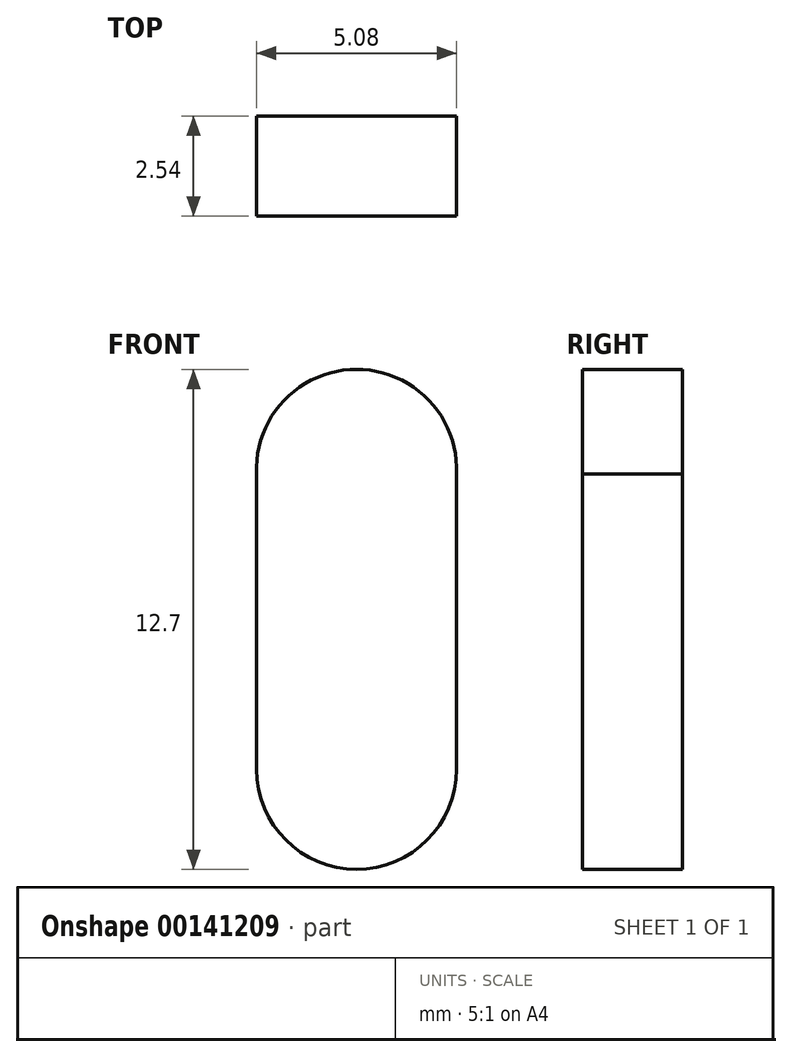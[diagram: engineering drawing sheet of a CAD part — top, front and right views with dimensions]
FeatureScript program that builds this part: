
annotation { "Feature Type Name" : "Feature", "Feature Type Description" : "" }
export const myFeature = defineFeature(function(context is Context, id is Id, definition is map)
    precondition{}
    {
        {
            var Q0;
            Q0=qCreatedBy(makeId("Front.planeOp"),FACE);
            var sketch = newSketch(context, id + "F0", { "sketchPlane" : qUnion([Q0])});
            skArc(sketch, "E0", {"start": v(5.08, 0) * mm, "mid": v(2.54, 2.65) * mm, "end": v(0, 0) * mm});
            skLineSegment(sketch, "E1", {"start": v(0, 0) * mm, "end": v(0, -7.5) * mm});
            skLineSegment(sketch, "E2", {"start": v(5.08, 0) * mm, "end": v(5.08, -7.5) * mm});
            skArc(sketch, "E3", {"start": v(0, -7.5) * mm, "mid": v(2.54, -10.05) * mm, "end": v(5.08, -7.5) * mm});
            skSolve(sketch);
        }
        {
            var Q0;
            Q0 = qSketchRegion(id + "F0", true);
            extrude(context, id + "F1", {"entities" : qUnion([Q0]), "depth" : 2.54 * mm});
        }
    });
